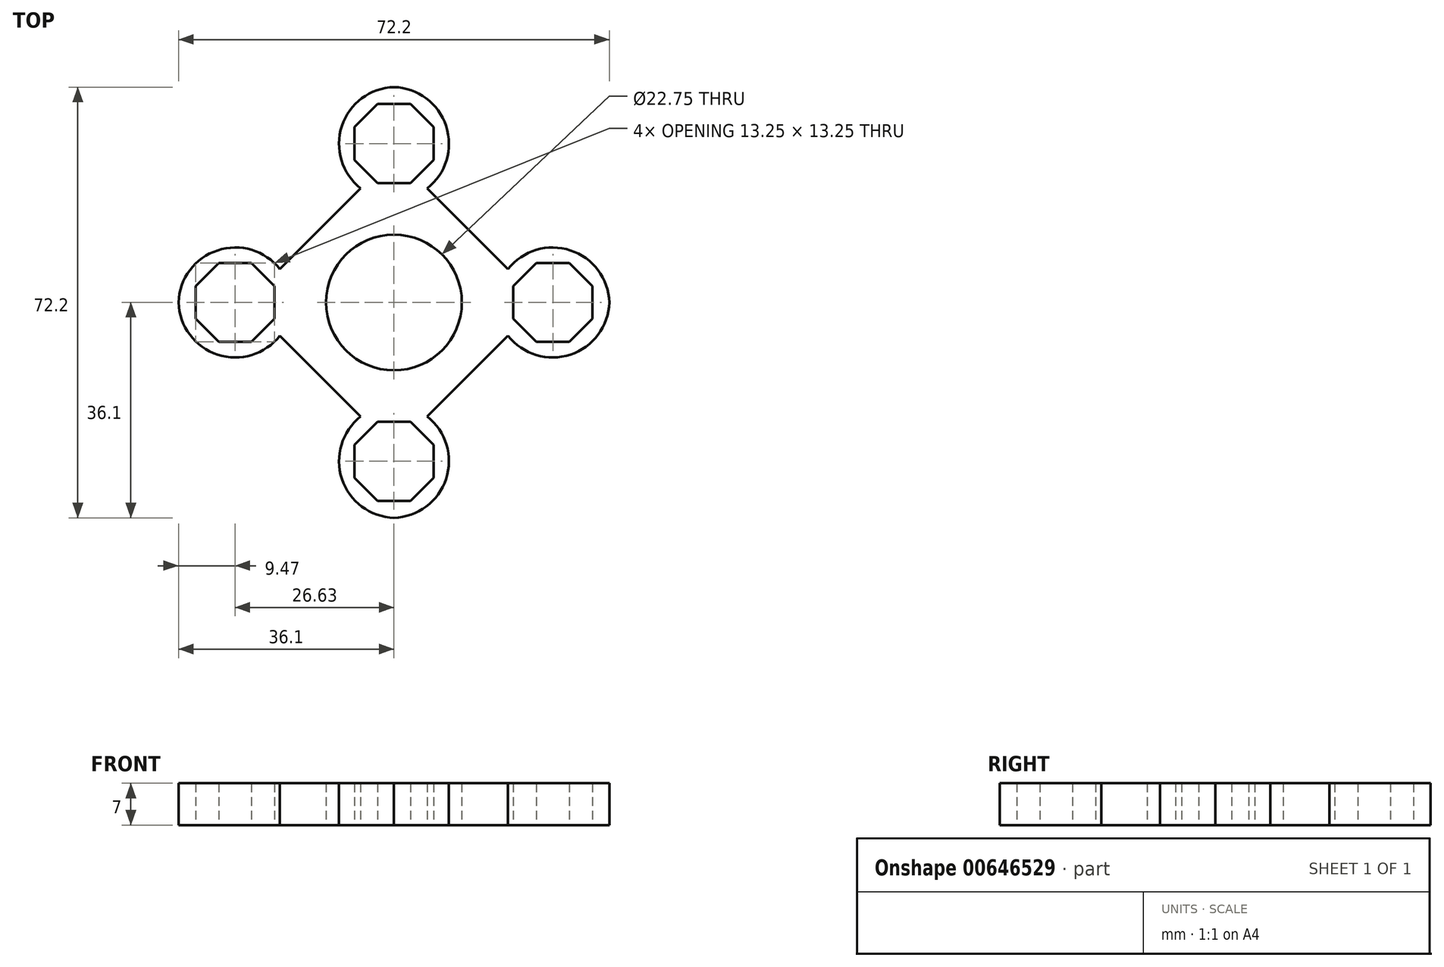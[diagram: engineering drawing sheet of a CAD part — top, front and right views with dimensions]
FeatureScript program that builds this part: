
annotation { "Feature Type Name" : "Feature", "Feature Type Description" : "" }
export const myFeature = defineFeature(function(context is Context, id is Id, definition is map)
    precondition{}
    {
        {
            var Q0;
            Q0=qCreatedBy(makeId("Top.planeOp"),FACE);
            var sketch = newSketch(context, id + "F0", { "sketchPlane" : qUnion([Q0])});
            skCircle(sketch, "E0.cCircle", {"center": v(0, 0) * mm, "radius": 13.5 * mm, "construction": true});
            skLineSegment(sketch, "E0.0", {"start": v(13.5, 5.6) * mm, "end": v(13.5, -5.6) * mm});
            skLineSegment(sketch, "E0.1", {"start": v(13.5, -5.6) * mm, "end": v(5.6, -13.5) * mm});
            skLineSegment(sketch, "E0.2", {"start": v(5.6, -13.5) * mm, "end": v(-5.6, -13.5) * mm});
            skLineSegment(sketch, "E0.3", {"start": v(-5.6, -13.5) * mm, "end": v(-13.5, -5.6) * mm});
            skLineSegment(sketch, "E0.4", {"start": v(-13.5, -5.6) * mm, "end": v(-13.5, 5.6) * mm});
            skLineSegment(sketch, "E0.5", {"start": v(-13.5, 5.6) * mm, "end": v(-5.6, 13.5) * mm});
            skLineSegment(sketch, "E0.6", {"start": v(-5.6, 13.5) * mm, "end": v(5.6, 13.5) * mm});
            skLineSegment(sketch, "E0.7", {"start": v(5.6, 13.5) * mm, "end": v(13.5, 5.6) * mm});
            skPoint(sketch, "E0.0.midPoint", {"position": v(13.5, 0) * mm});
            skCircle(sketch, "E1", {"center": v(0, 0) * mm, "radius": 11.38 * mm});
            skCircle(sketch, "E2.cCircle", {"center": v(0, 26.63) * mm, "radius": 6.62 * mm, "construction": true});
            skLineSegment(sketch, "E2.0", {"start": v(6.62, 29.37) * mm, "end": v(6.62, 23.89) * mm});
            skLineSegment(sketch, "E2.1", {"start": v(6.63, 23.89) * mm, "end": v(2.74, 20) * mm});
            skLineSegment(sketch, "E2.2", {"start": v(2.74, 20) * mm, "end": v(-2.74, 20) * mm});
            skLineSegment(sketch, "E2.3", {"start": v(-2.74, 20) * mm, "end": v(-6.62, 23.89) * mm});
            skLineSegment(sketch, "E2.4", {"start": v(-6.62, 23.89) * mm, "end": v(-6.62, 29.37) * mm});
            skLineSegment(sketch, "E2.5", {"start": v(-6.63, 29.37) * mm, "end": v(-2.74, 33.26) * mm});
            skLineSegment(sketch, "E2.6", {"start": v(-2.74, 33.26) * mm, "end": v(2.74, 33.26) * mm});
            skLineSegment(sketch, "E2.7", {"start": v(2.74, 33.26) * mm, "end": v(6.62, 29.37) * mm});
            skPoint(sketch, "E2.0.midPoint", {"position": v(6.62, 26.63) * mm});
            skArc(sketch, "E3", {"start": v(4.3, 18.25) * mm, "mid": v(8.95, 28.82) * mm, "end": v(0, 36.1) * mm});
            skArc(sketch, "E4.MirrorCS", {"start": v(-4.3, 18.25) * mm, "mid": v(-8.95, 28.82) * mm, "end": v(0, 36.1) * mm});
            skLineSegment(sketch, "E5", {"start": v(5.6, 13.5) * mm, "end": v(5.6, 19.12) * mm});
            skLineSegment(sketch, "E6", {"start": v(5.6, 19.12) * mm, "end": v(5.6, 13.5) * mm});
            skLineSegment(sketch, "E7", {"start": v(-5.6, 13.5) * mm, "end": v(-5.6, 19.12) * mm});
            skArc(sketch, "E8.1.0", {"start": v(-18.25, -4.3) * mm, "mid": v(-28.82, -8.95) * mm, "end": v(-36.1, 0) * mm});
            skLineSegment(sketch, "E8.1.1", {"start": v(-13.5, -5.6) * mm, "end": v(-19.12, -5.6) * mm});
            skLineSegment(sketch, "E8.1.2", {"start": v(-19.12, 5.6) * mm, "end": v(-13.5, 5.6) * mm});
            skLineSegment(sketch, "E8.1.3", {"start": v(-20, -2.74) * mm, "end": v(-23.89, -6.62) * mm});
            skCircle(sketch, "E8.1.5", {"center": v(-26.63, 0) * mm, "radius": 6.62 * mm, "construction": true});
            skPoint(sketch, "E8.1.6", {"position": v(-26.63, 6.63) * mm});
            skArc(sketch, "E8.1.7", {"start": v(-18.25, 4.3) * mm, "mid": v(-28.82, 8.95) * mm, "end": v(-36.1, 0) * mm});
            skLineSegment(sketch, "E8.1.8", {"start": v(-13.5, 5.6) * mm, "end": v(-19.12, 5.6) * mm});
            skLineSegment(sketch, "E8.1.9", {"start": v(-23.89, -6.62) * mm, "end": v(-29.37, -6.62) * mm});
            skLineSegment(sketch, "E8.1.10", {"start": v(-29.37, -6.63) * mm, "end": v(-33.26, -2.74) * mm});
            skLineSegment(sketch, "E8.1.11", {"start": v(-29.37, 6.62) * mm, "end": v(-23.89, 6.62) * mm});
            skLineSegment(sketch, "E8.1.12", {"start": v(-20, 2.74) * mm, "end": v(-20, -2.74) * mm});
            skLineSegment(sketch, "E8.1.13", {"start": v(-23.89, 6.63) * mm, "end": v(-20, 2.74) * mm});
            skLineSegment(sketch, "E8.1.14", {"start": v(-33.26, 2.74) * mm, "end": v(-29.37, 6.63) * mm});
            skLineSegment(sketch, "E8.1.15", {"start": v(-33.26, -2.74) * mm, "end": v(-33.26, 2.74) * mm});
            skArc(sketch, "E8.2.0", {"start": v(4.3, -18.25) * mm, "mid": v(8.95, -28.82) * mm, "end": v(0, -36.1) * mm});
            skLineSegment(sketch, "E8.2.1", {"start": v(5.6, -13.5) * mm, "end": v(5.6, -19.12) * mm});
            skLineSegment(sketch, "E8.2.2", {"start": v(-5.6, -19.12) * mm, "end": v(-5.6, -13.5) * mm});
            skLineSegment(sketch, "E8.2.3", {"start": v(2.74, -20) * mm, "end": v(6.62, -23.89) * mm});
            skCircle(sketch, "E8.2.5", {"center": v(0, -26.63) * mm, "radius": 6.62 * mm, "construction": true});
            skPoint(sketch, "E8.2.6", {"position": v(-6.63, -26.63) * mm});
            skArc(sketch, "E8.2.7", {"start": v(-4.3, -18.25) * mm, "mid": v(-8.95, -28.82) * mm, "end": v(0, -36.1) * mm});
            skLineSegment(sketch, "E8.2.8", {"start": v(-5.6, -13.5) * mm, "end": v(-5.6, -19.12) * mm});
            skLineSegment(sketch, "E8.2.9", {"start": v(6.62, -23.89) * mm, "end": v(6.62, -29.37) * mm});
            skLineSegment(sketch, "E8.2.10", {"start": v(6.63, -29.37) * mm, "end": v(2.74, -33.26) * mm});
            skLineSegment(sketch, "E8.2.11", {"start": v(-6.63, -29.37) * mm, "end": v(-6.62, -23.89) * mm});
            skLineSegment(sketch, "E8.2.12", {"start": v(-2.74, -20) * mm, "end": v(2.74, -20) * mm});
            skLineSegment(sketch, "E8.2.13", {"start": v(-6.63, -23.89) * mm, "end": v(-2.74, -20) * mm});
            skLineSegment(sketch, "E8.2.14", {"start": v(-2.74, -33.26) * mm, "end": v(-6.63, -29.37) * mm});
            skLineSegment(sketch, "E8.2.15", {"start": v(2.74, -33.26) * mm, "end": v(-2.74, -33.26) * mm});
            skArc(sketch, "E8.3.0", {"start": v(18.25, 4.3) * mm, "mid": v(28.82, 8.95) * mm, "end": v(36.1, 0) * mm});
            skLineSegment(sketch, "E8.3.1", {"start": v(13.5, 5.6) * mm, "end": v(19.12, 5.6) * mm});
            skLineSegment(sketch, "E8.3.2", {"start": v(19.12, -5.6) * mm, "end": v(13.5, -5.6) * mm});
            skLineSegment(sketch, "E8.3.3", {"start": v(20, 2.74) * mm, "end": v(23.89, 6.62) * mm});
            skCircle(sketch, "E8.3.5", {"center": v(26.63, 0) * mm, "radius": 6.62 * mm, "construction": true});
            skPoint(sketch, "E8.3.6", {"position": v(26.63, -6.62) * mm});
            skArc(sketch, "E8.3.7", {"start": v(18.25, -4.3) * mm, "mid": v(28.82, -8.95) * mm, "end": v(36.1, 0) * mm});
            skLineSegment(sketch, "E8.3.8", {"start": v(13.5, -5.6) * mm, "end": v(19.12, -5.6) * mm});
            skLineSegment(sketch, "E8.3.9", {"start": v(23.89, 6.62) * mm, "end": v(29.37, 6.62) * mm});
            skLineSegment(sketch, "E8.3.10", {"start": v(29.37, 6.63) * mm, "end": v(33.26, 2.74) * mm});
            skLineSegment(sketch, "E8.3.11", {"start": v(29.37, -6.63) * mm, "end": v(23.89, -6.63) * mm});
            skLineSegment(sketch, "E8.3.12", {"start": v(20, -2.74) * mm, "end": v(20, 2.74) * mm});
            skLineSegment(sketch, "E8.3.13", {"start": v(23.89, -6.63) * mm, "end": v(20, -2.74) * mm});
            skLineSegment(sketch, "E8.3.14", {"start": v(33.26, -2.74) * mm, "end": v(29.37, -6.62) * mm});
            skLineSegment(sketch, "E8.3.15", {"start": v(33.26, 2.74) * mm, "end": v(33.26, -2.74) * mm});
            skLineSegment(sketch, "E9", {"start": v(-5.6, 19.12) * mm, "end": v(-19.12, 5.6) * mm});
            skLineSegment(sketch, "E10", {"start": v(-19.12, -5.6) * mm, "end": v(-5.6, -19.12) * mm});
            skLineSegment(sketch, "E11", {"start": v(5.6, -19.12) * mm, "end": v(19.12, -5.6) * mm});
            skLineSegment(sketch, "E12", {"start": v(19.12, 5.6) * mm, "end": v(5.6, 19.12) * mm});
            skSolve(sketch);
        }
        {
            var Q0;
            Q0=makeQuery(id+"F0.imprint","IMPRINT",FACE,{"disambiguationData":[TD([[makeQuery(id+"F0.imprint","IMPRINT",EDGE,{"derivedFrom":sQuery(id+"F0.wireOp",EDGE,"E0.3")}),1.0]])]});
            var Q1;
            Q1=makeQuery(id+"F0.imprint","IMPRINT",FACE,{"disambiguationData":[TD([[makeQuery(id+"F0.imprint","IMPRINT",EDGE,{"derivedFrom":sQuery(id+"F0.wireOp",EDGE,"E0.5")}),1.0]])]});
            var Q2;
            Q2=makeQuery(id+"F0.imprint","IMPRINT",FACE,{"disambiguationData":[TD([[makeQuery(id+"F0.imprint","IMPRINT",EDGE,{"derivedFrom":sQuery(id+"F0.wireOp",EDGE,"E0.6")}),1.0]])]});
            var Q3;
            {var subQ4=sQuery(id+"F0.wireOp",EDGE,"E8.1.1");Q3=makeQuery(id+"F0.imprint","IMPRINT",FACE,{"disambiguationData":[TD([[makeQuery(id+"F0.imprint","IMPRINT",EDGE,{"derivedFrom":subQ4}),-1.0]])]});}
            var Q4;
            Q4=makeQuery(id+"F0.imprint","IMPRINT",FACE,{"disambiguationData":[TD([[makeQuery(id+"F0.imprint","IMPRINT",EDGE,{"derivedFrom":sQuery(id+"F0.wireOp",EDGE,"E0.7")}),1.0]])]});
            var Q5;
            {var subQ4=sQuery(id+"F0.wireOp",EDGE,"E8.3.1");Q5=makeQuery(id+"F0.imprint","IMPRINT",FACE,{"disambiguationData":[TD([[makeQuery(id+"F0.imprint","IMPRINT",EDGE,{"derivedFrom":subQ4}),-1.0]])]});}
            var Q6;
            Q6=makeQuery(id+"F0.imprint","IMPRINT",FACE,{"disambiguationData":[TD([[makeQuery(id+"F0.imprint","IMPRINT",EDGE,{"derivedFrom":sQuery(id+"F0.wireOp",EDGE,"E0.1")}),1.0]])]});
            var Q7;
            {var subQ4=sQuery(id+"F0.wireOp",EDGE,"E8.2.1");Q7=makeQuery(id+"F0.imprint","IMPRINT",FACE,{"disambiguationData":[TD([[makeQuery(id+"F0.imprint","IMPRINT",EDGE,{"derivedFrom":subQ4}),-1.0]])]});}
            var Q8;
            Q8=makeQuery(id+"F0.imprint","IMPRINT",FACE,{"disambiguationData":[TD([[makeQuery(id+"F0.imprint","IMPRINT",EDGE,{"derivedFrom":sQuery(id+"F0.wireOp",EDGE,"E0.1")}),-1.0]])]});
            extrude(context, id + "F1", {"entities" : qUnion([Q0, Q1, Q2, Q3, Q4, Q5, Q6, Q7, Q8]), "depth" : 7 * mm, "offsetDistance" : 25 * mm});
        }
    });
